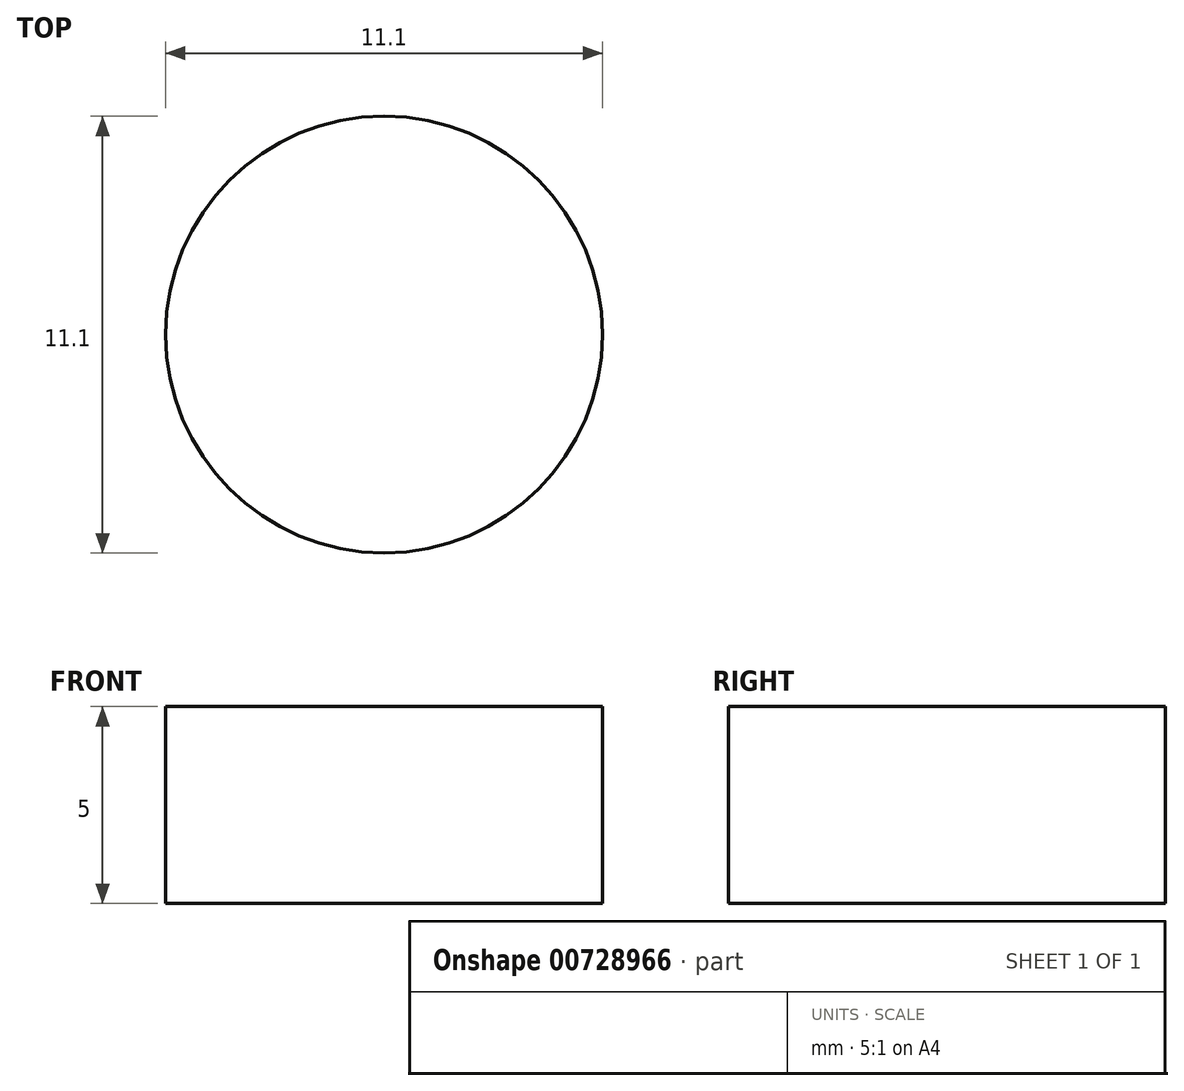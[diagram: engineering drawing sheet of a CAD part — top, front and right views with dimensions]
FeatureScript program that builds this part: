
annotation { "Feature Type Name" : "Feature", "Feature Type Description" : "" }
export const myFeature = defineFeature(function(context is Context, id is Id, definition is map)
    precondition{}
    {
        {
            var Q0;
            Q0=qCreatedBy(makeId("Top.planeOp"),FACE);
            var sketch = newSketch(context, id + "F0", { "sketchPlane" : qUnion([Q0])});
            skCircle(sketch, "E0", {"center": v(0, 0) * mm, "radius": 5.55 * mm});
            skSolve(sketch);
        }
        {
            var Q0;
            Q0=makeQuery(id+"F0.imprint","IMPRINT",FACE,{"disambiguationData":[TD([[makeQuery(id+"F0.imprint","IMPRINT",EDGE,{"derivedFrom":sQuery(id+"F0.wireOp",EDGE,"E0")}),1.0]])]});
            extrude(context, id + "F1", {"entities" : qUnion([Q0]), "depth" : 5 * mm, "offsetDistance" : 25.4 * mm});
        }
    });
